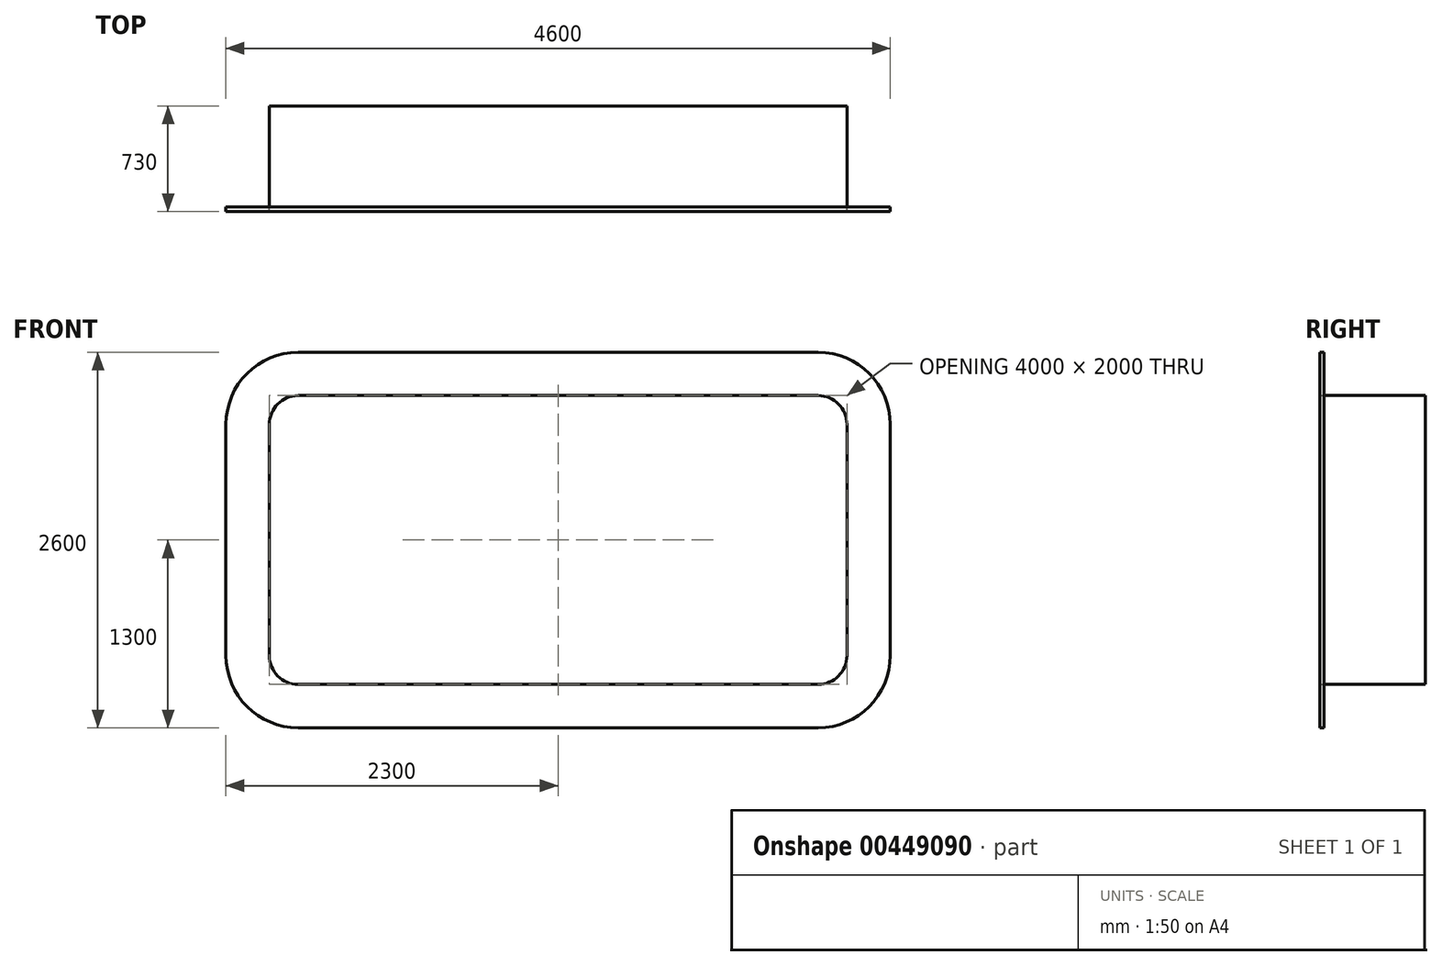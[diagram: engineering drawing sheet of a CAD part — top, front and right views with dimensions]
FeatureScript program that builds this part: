
annotation { "Feature Type Name" : "Feature", "Feature Type Description" : "" }
export const myFeature = defineFeature(function(context is Context, id is Id, definition is map)
    precondition{}
    {
        {
            var Q0;
            Q0=qCreatedBy(makeId("Front.planeOp"),FACE);
            var sketch = newSketch(context, id + "F0", { "sketchPlane" : qUnion([Q0])});
            skLineSegment(sketch, "E0.bottom", {"start": v(1832.41, -2970.42) * mm, "end": v(-1767.59, -2970.42) * mm});
            skLineSegment(sketch, "E0.top", {"start": v(1832.41, -4970.42) * mm, "end": v(-1767.59, -4970.42) * mm});
            skLineSegment(sketch, "E0.left", {"start": v(2032.41, -3170.42) * mm, "end": v(2032.41, -4770.42) * mm});
            skLineSegment(sketch, "E0.right", {"start": v(-1967.59, -3170.42) * mm, "end": v(-1967.59, -4770.42) * mm});
            skPoint(sketch, "E0.middle", {"position": v(32.41, -3970.42) * mm});
            skPoint(sketch, "E1.visualSharp", {"position": v(-1967.59, -2970.42) * mm});
            skArc(sketch, "E1.filletArc", {"start": v(-1767.59, -2970.42) * mm, "mid": v(-1909, -3029) * mm, "end": v(-1967.59, -3170.42) * mm});
            skPoint(sketch, "E2.visualSharp", {"position": v(2032.41, -2970.42) * mm});
            skArc(sketch, "E2.filletArc", {"start": v(2032.41, -3170.42) * mm, "mid": v(1973.84, -3029) * mm, "end": v(1832.41, -2970.42) * mm});
            skPoint(sketch, "E3.visualSharp", {"position": v(-1967.59, -4970.42) * mm});
            skArc(sketch, "E3.filletArc", {"start": v(-1967.59, -4770.42) * mm, "mid": v(-1909, -4911.84) * mm, "end": v(-1767.59, -4970.42) * mm});
            skPoint(sketch, "E4.visualSharp", {"position": v(2032.41, -4970.42) * mm});
            skArc(sketch, "E4.filletArc", {"start": v(1832.41, -4970.42) * mm, "mid": v(1973.84, -4911.84) * mm, "end": v(2032.41, -4770.42) * mm});
            skArc(sketch, "E5.0", {"start": v(-1767.59, -2670.42) * mm, "mid": v(-2121.14, -2816.86) * mm, "end": v(-2267.59, -3170.42) * mm});
            skLineSegment(sketch, "E5.1", {"start": v(1832.41, -2670.42) * mm, "end": v(-1767.59, -2670.42) * mm});
            skLineSegment(sketch, "E5.2", {"start": v(-2267.59, -3170.42) * mm, "end": v(-2267.59, -4770.42) * mm});
            skArc(sketch, "E5.3", {"start": v(2332.41, -3170.42) * mm, "mid": v(2185.97, -2816.86) * mm, "end": v(1832.41, -2670.42) * mm});
            skArc(sketch, "E5.4", {"start": v(-2267.59, -4770.42) * mm, "mid": v(-2121.14, -5123.97) * mm, "end": v(-1767.59, -5270.42) * mm});
            skLineSegment(sketch, "E5.5", {"start": v(1832.41, -5270.42) * mm, "end": v(-1767.59, -5270.42) * mm});
            skArc(sketch, "E5.6", {"start": v(1832.41, -5270.42) * mm, "mid": v(2185.97, -5123.97) * mm, "end": v(2332.41, -4770.42) * mm});
            skLineSegment(sketch, "E5.7", {"start": v(2332.41, -3170.42) * mm, "end": v(2332.41, -4770.42) * mm});
            skSolve(sketch);
        }
        {
            var Q0;
            Q0=makeQuery(id+"F0.imprint","IMPRINT",FACE,{"disambiguationData":[TD([[makeQuery(id+"F0.imprint","IMPRINT",EDGE,{"derivedFrom":sQuery(id+"F0.wireOp",EDGE,"E0.bottom")}),-1.0]])]});
            extrude(context, id + "F1", {"entities" : qUnion([Q0]), "depth" : 30 * mm});
        }
        {
            var Q0;
            Q0=makeQuery(id+"F1.opExtrude","CAP_FACE",FACE,{"disambiguationData":[OSD([sQuery(id+"F0.wireOp",EDGE,"E0.bottom"),sQuery(id+"F0.wireOp",EDGE,"E0.top"),sQuery(id+"F0.wireOp",EDGE,"E0.left"),sQuery(id+"F0.wireOp",EDGE,"E0.right"),sQuery(id+"F0.wireOp",EDGE,"E1.filletArc"),sQuery(id+"F0.wireOp",EDGE,"E2.filletArc"),sQuery(id+"F0.wireOp",EDGE,"E3.filletArc"),sQuery(id+"F0.wireOp",EDGE,"E4.filletArc"),sQuery(id+"F0.wireOp",EDGE,"E5.0"),sQuery(id+"F0.wireOp",EDGE,"E5.1"),sQuery(id+"F0.wireOp",EDGE,"E5.2"),sQuery(id+"F0.wireOp",EDGE,"E5.3"),sQuery(id+"F0.wireOp",EDGE,"E5.4"),sQuery(id+"F0.wireOp",EDGE,"E5.5"),sQuery(id+"F0.wireOp",EDGE,"E5.6"),sQuery(id+"F0.wireOp",EDGE,"E5.7")])],"isStart":true});
            var sketch = newSketch(context, id + "F2", { "sketchPlane" : qUnion([Q0])});
            skSolve(sketch);
        }
        {
            var Q0;
            Q0=makeQuery(id+"F2.imprint","IMPRINT",FACE,{"disambiguationData":[TD([[makeQuery(id+"F2.imprint","IMPRINT",EDGE,{"derivedFrom":makeQuery(id+"F1.opExtrude","CAP_EDGE",EDGE,{"disambiguationData":[OSD([sQuery(id+"F0.wireOp",EDGE,"E0.bottom")])],"isStart":true})}),-1.0]])]});
            extrude(context, id + "F3", {"entities" : qUnion([Q0]), "depth" : 700 * mm});
        }
    });
